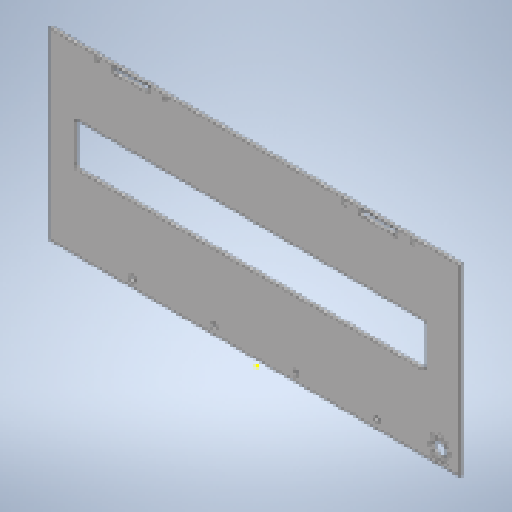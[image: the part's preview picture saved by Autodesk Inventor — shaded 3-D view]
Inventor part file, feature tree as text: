
AUTODESK INVENTOR PART (.ipt)
format: ipt  version: 2024 (Build 280153000, 153)  size: 278,528 bytes
history: native  units: mm
features: reference x18, other x8, extrude x3, sketch x3, fillet x2
ambient origin geometry x8: Origin, YZ Plane, XZ Plane, XY Plane, X Axis, Y Axis, Z Axis, Center Point
bodies: Body1 (feature_tree)
feature tree (34):
  other  "ソリッド1"
  extrude  "押し出し1"  Depth=3.2mm
  fillet  "フィレット1"  Radius=3.2mm
  fillet  "フィレット2"  Radius=3.2mm
  extrude  "押し出し3"  Depth=3.2mm
  extrude  "押し出し6"  Depth=2.2mm
  sketch  "スケッチ1"
  reference  "参照1"
  reference  "参照2"
  reference  "参照3"
  reference  "参照4"
  reference  "参照5"
  reference  "参照6"
  reference  "参照7"
  reference  "参照8"
  reference  "参照9"
  reference  "参照10"
  reference  "参照11"
  reference  "参照12"
  reference  "参照13"
  reference  "参照14"
  reference  "参照15"
  reference  "参照16"
  reference  "参照17"
  sketch  "スケッチ4"
  sketch  "スケッチ7"
  reference  "参照27"
  other  "<userpath>\OneDrive\ドキュメント\Inventor\Vixen\leg.iam"
  other  "leg.iam"
  other  "SR4-500_On:1"
  other  "wall:1"
  other  "01029_01042_LowheightServoHorn:1"
  other  "sokumen:1"
  other  "free:2"
